# Revit family: Faucet-Lavatory-KOHLER-Strayt-K-37329IN
name_source: partatom
category: Plumbing Fixtures
revit_build: Autodesk Revit 2017 (Build: 20160225_1515(x64)
units: mm (PartAtom-declared; Revit-internal decimal feet)

## family parameters
Cut with Voids When Loaded = No
Host = Face
OmniClass Number = 23.31.11.00
Part Type = Normal
Room Calculation Point = No
Round Connector Dimension = Use Diameter
Shared = No

## types (4) — shared parameters
ADA Compliant = No
Assembly Code = D2010
CW Connection = Yes
Cold Water Inlet = Cold Water Inlet
Date Modified = 09/16/2020
Default Elevation = 36"
Faucet Hole Spacing = 0"
Flow Rate = 0 GPM
HW Connection = Yes
Handle Clearance = 3 1/4"
Height = 12 5/8"
Hot Water Inlet = Hot Water Inlet
Length = 5 3/16"
Manufacturer = KOHLER Co.
Master Format 2014 = 22 41 39
Master Format 2014 Name = Residential Faucets, Supplies, and Trim
Material = Premium Metal Construction
Pressure = 0.00 psi
Product Documentation Link = http://resources.kohler.com
Product Name = Strayt
Spout Reach = 5 3/16"
URL = https://www.kohler.co.in
Vent Connection = No
Waste Connection = No
Waste Water Outlet = Waste Water Outlet
WaterSense Certified = No
Width = 1 13/16"

## per-type parameters (varying)
| type | Description | Drain Included | Finish | Lift Rod | Model | No Lift Rod | Not Drain Included | Product Page URL | Type |
| With Drain,AF-Vibrant French Gold | SC LAV FAUCET WITH DRAIN | Yes | Kohler-Metal-AF-Vibrant_French_Gold | Yes | K-37329IN-4-AF | No | No |  | 1 |
| With Drain,CP-Polished Chrome | SC LAV FAUCET WITH DRAIN | Yes | Kohler-Metal-CP-Polished_Chrome | Yes | K-37329IN-4-CP | No | No |  | 2 |
| Without Drain,CP-Polished Chrome | SC LAV FAUCET W/O DRAIN | No | Kohler-Metal-CP-Polished_Chrome | No | K-37329IN-4ND-CP | Yes | Yes | https://www.kohler.co.in | 3 |
| Without Drain-AF-Vibrant French Gold | SC LAV FAUCET W/O DRAIN | No | Kohler-Metal-AF-Vibrant_French_Gold | No | K-37329IN-4ND-AF | Yes | Yes | https://www.kohler.co.in | 4 |

## geometry (parser evidence)
native form markers: Sweep x5
no freeform markers — native parametric forms only
